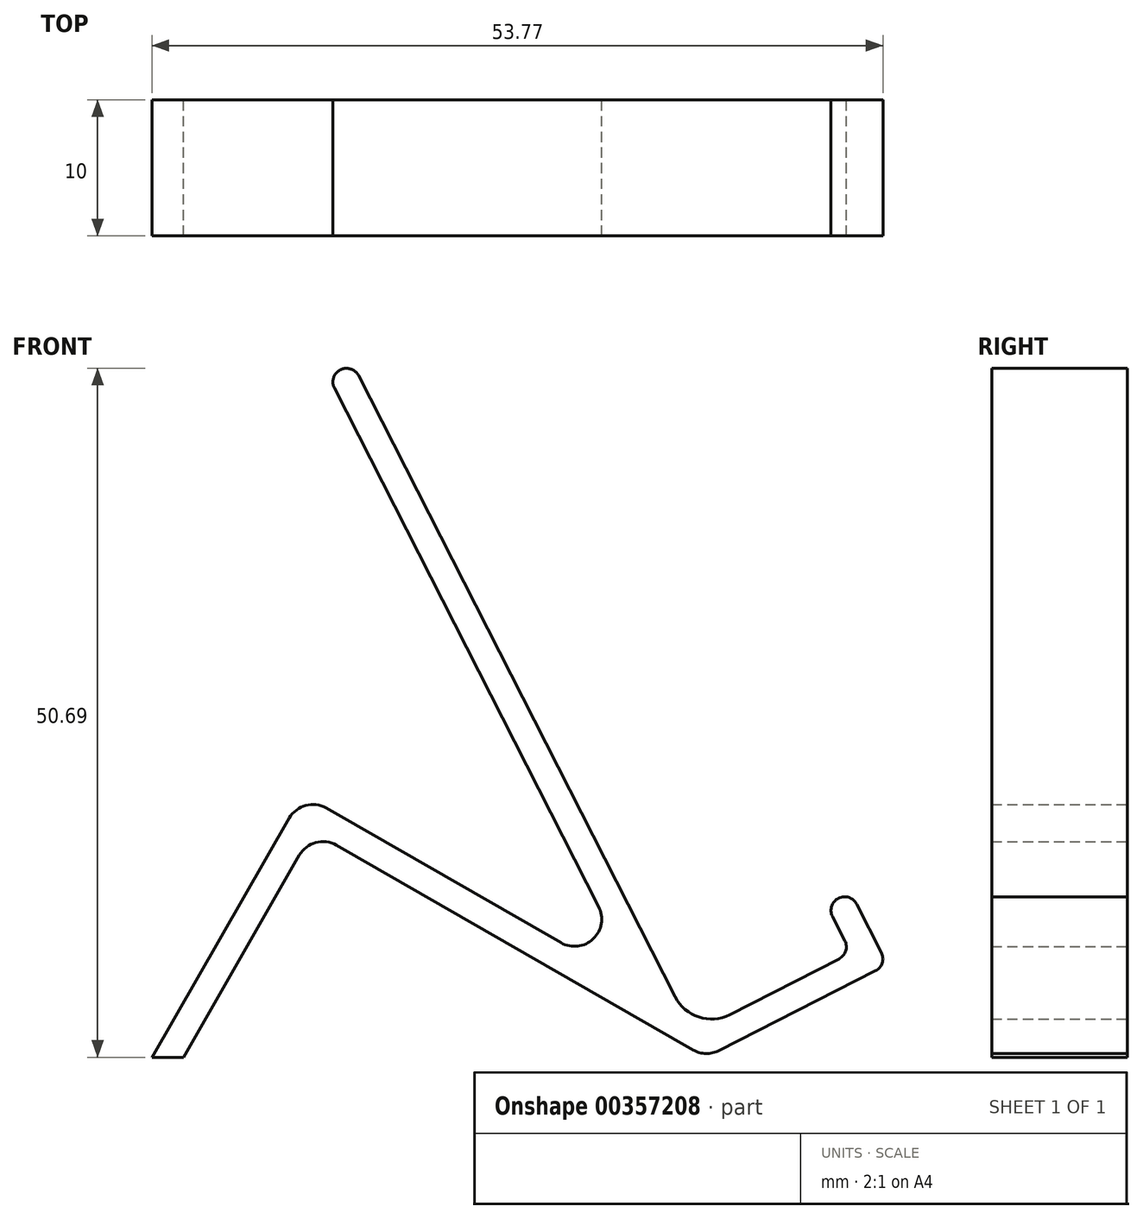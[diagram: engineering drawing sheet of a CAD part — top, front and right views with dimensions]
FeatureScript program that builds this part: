
annotation { "Feature Type Name" : "Feature", "Feature Type Description" : "" }
export const myFeature = defineFeature(function(context is Context, id is Id, definition is map)
    precondition{}
    {
        {
            var Q0;
            Q0=qCreatedBy(makeId("Front.planeOp"),FACE);
            var sketch = newSketch(context, id + "F0", { "sketchPlane" : qUnion([Q0])});
            skLineSegment(sketch, "E0", {"start": v(-25.55, 50.14) * mm, "end": v(-2.27, 4.46) * mm});
            skLineSegment(sketch, "E1", {"start": v(-0.94, 0.54) * mm, "end": v(-27.18, 15.6) * mm});
            skLineSegment(sketch, "E2", {"start": v(-29.91, 14.87) * mm, "end": v(-38.45, 0) * mm});
            skLineSegment(sketch, "E3", {"start": v(-26.44, 50.7) * mm, "end": v(-26.44, 50.7) * mm});
            skLineSegment(sketch, "E4", {"start": v(-27.33, 49.24) * mm, "end": v(-7.88, 11.07) * mm});
            skLineSegment(sketch, "E5", {"start": v(-10.66, 8.43) * mm, "end": v(-27.92, 18.34) * mm});
            skLineSegment(sketch, "E6", {"start": v(-30.65, 17.6) * mm, "end": v(-40.75, 0) * mm});
            skLineSegment(sketch, "E7", {"start": v(-40.75, 0) * mm, "end": v(-38.45, 0) * mm});
            skLineSegment(sketch, "E8", {"start": v(0.96, 0.5) * mm, "end": v(11.58, 5.9) * mm});
            skLineSegment(sketch, "E9", {"start": v(1.77, 3.14) * mm, "end": v(9.78, 7.23) * mm});
            skPoint(sketch, "E10.visualSharp", {"position": v(-0.9, 1.78) * mm});
            skArc(sketch, "E10.filletArc", {"start": v(-2.27, 4.46) * mm, "mid": v(-0.52, 2.96) * mm, "end": v(1.77, 3.14) * mm});
            skPoint(sketch, "E11.visualSharp", {"position": v(-4.83, 5.08) * mm});
            skArc(sketch, "E11.filletArc", {"start": v(-10.66, 8.43) * mm, "mid": v(-8.29, 8.71) * mm, "end": v(-7.88, 11.07) * mm});
            skPoint(sketch, "E12.visualSharp", {"position": v(-28.92, 16.6) * mm});
            skArc(sketch, "E12.filletArc", {"start": v(-27.18, 15.6) * mm, "mid": v(-28.7, 15.8) * mm, "end": v(-29.91, 14.87) * mm});
            skPoint(sketch, "E13.visualSharp", {"position": v(-29.66, 19.33) * mm});
            skArc(sketch, "E13.filletArc", {"start": v(-27.92, 18.34) * mm, "mid": v(-29.44, 18.53) * mm, "end": v(-30.65, 17.6) * mm});
            skPoint(sketch, "E14.visualSharp", {"position": v(-25.83, 50.7) * mm});
            skArc(sketch, "E14.filletArc", {"start": v(-25.55, 50.14) * mm, "mid": v(-25.92, 50.54) * mm, "end": v(-26.44, 50.7) * mm});
            skPoint(sketch, "E15.visualSharp", {"position": v(-28.07, 50.7) * mm});
            skArc(sketch, "E15.filletArc", {"start": v(-26.44, 50.7) * mm, "mid": v(-27.3, 50.21) * mm, "end": v(-27.33, 49.24) * mm});
            skPoint(sketch, "E16.visualSharp", {"position": v(0, 0) * mm});
            skArc(sketch, "E16.filletArc", {"start": v(-0.94, 0.54) * mm, "mid": v(0, 0.27) * mm, "end": v(0.96, 0.5) * mm});
            skLineSegment(sketch, "E17.bottom", {"start": v(11.58, 5.9) * mm, "end": v(12.47, 6.36) * mm});
            skLineSegment(sketch, "E17.top", {"start": v(9.75, 11.7) * mm, "end": v(9.75, 11.7) * mm});
            skLineSegment(sketch, "E17.left", {"start": v(10.22, 8.57) * mm, "end": v(9.31, 10.36) * mm});
            skLineSegment(sketch, "E17.right", {"start": v(12.91, 7.7) * mm, "end": v(11.1, 11.26) * mm});
            skPoint(sketch, "E18.start.orphan", {"position": v(11.58, 5.9) * mm});
            skPoint(sketch, "E19.visualSharp", {"position": v(10.68, 7.68) * mm});
            skArc(sketch, "E19.filletArc", {"start": v(9.78, 7.23) * mm, "mid": v(10.28, 7.81) * mm, "end": v(10.22, 8.57) * mm});
            skPoint(sketch, "E20.visualSharp", {"position": v(13.37, 6.8) * mm});
            skArc(sketch, "E20.filletArc", {"start": v(12.47, 6.36) * mm, "mid": v(12.97, 6.94) * mm, "end": v(12.91, 7.7) * mm});
            skPoint(sketch, "E21.visualSharp", {"position": v(8.86, 11.25) * mm});
            skArc(sketch, "E21.filletArc", {"start": v(9.75, 11.7) * mm, "mid": v(9.25, 11.12) * mm, "end": v(9.31, 10.36) * mm});
            skPoint(sketch, "E22.visualSharp", {"position": v(10.64, 12.16) * mm});
            skArc(sketch, "E22.filletArc", {"start": v(11.1, 11.26) * mm, "mid": v(10.51, 11.76) * mm, "end": v(9.75, 11.7) * mm});
            skSolve(sketch);
        }
        {
            var Q0;
            Q0=makeQuery(id+"F0.imprint","IMPRINT",FACE,{"disambiguationData":[TD([[makeQuery(id+"F0.imprint","IMPRINT",EDGE,{"derivedFrom":sQuery(id+"F0.wireOp",EDGE,"E0")}),-1.0]])]});
            extrude(context, id + "F1", {"entities" : qUnion([Q0]), "depth" : 10 * mm});
        }
    });
